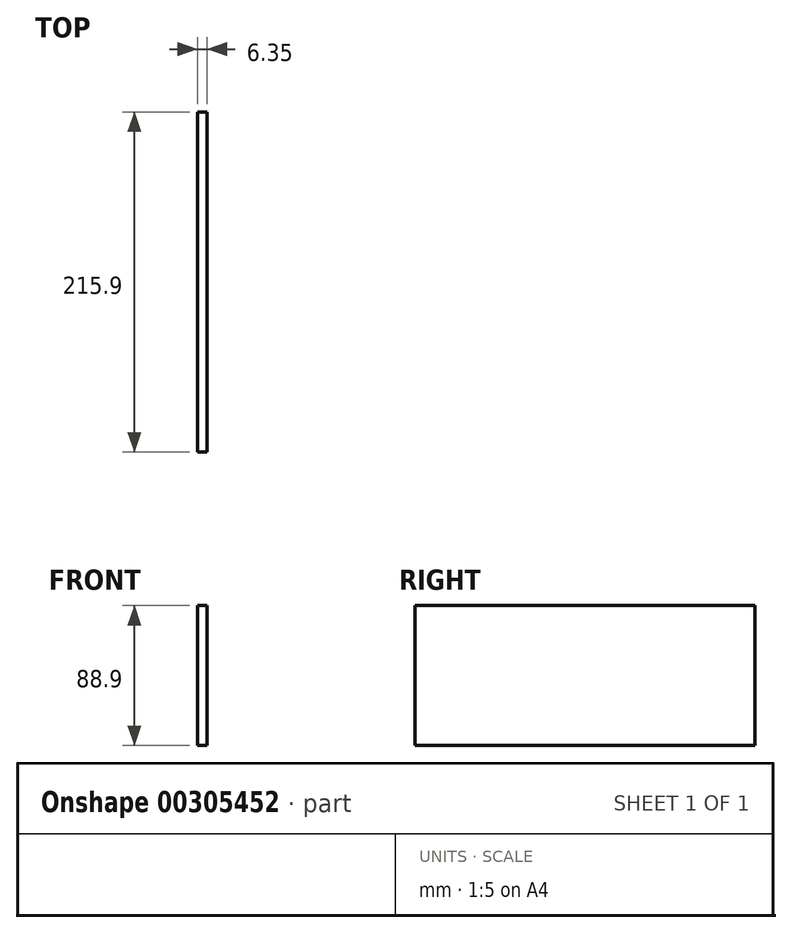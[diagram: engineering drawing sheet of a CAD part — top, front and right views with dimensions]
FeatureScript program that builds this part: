
annotation { "Feature Type Name" : "Feature", "Feature Type Description" : "" }
export const myFeature = defineFeature(function(context is Context, id is Id, definition is map)
    precondition{}
    {
        {
            var Q0;
            Q0=qCreatedBy(makeId("Right.planeOp"),FACE);
            var sketch = newSketch(context, id + "F0", { "sketchPlane" : qUnion([Q0])});
            skLineSegment(sketch, "E0.bottom", {"start": v(-162.88, 88.9) * mm, "end": v(53.02, 88.9) * mm});
            skLineSegment(sketch, "E0.top", {"start": v(-162.88, 0) * mm, "end": v(53.02, 0) * mm});
            skLineSegment(sketch, "E0.left", {"start": v(-162.88, 88.9) * mm, "end": v(-162.88, 0) * mm});
            skLineSegment(sketch, "E0.right", {"start": v(53.02, 88.9) * mm, "end": v(53.02, 0) * mm});
            skSolve(sketch);
        }
        {
            var Q0;
            Q0 = qSketchRegion(id + "F0", true);
            extrude(context, id + "F1", {"entities" : qUnion([Q0]), "depth" : 6.35 * mm});
        }
    });
